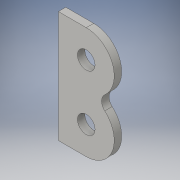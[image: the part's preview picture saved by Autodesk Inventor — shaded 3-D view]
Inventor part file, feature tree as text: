
AUTODESK INVENTOR PART (.ipt)
format: ipt  version: 2016 (Build 200138000, 138)  size: 114,688 bytes
history: native  units: in
note: dims shown in document units (in); Inventor stores cm internally (conversion verified against a paired STEP export)
features: extrude x1, sketch x1
ambient origin geometry x8: Origin, YZ Plane, XZ Plane, XY Plane, X Axis, Y Axis, Z Axis, Center Point
bodies: Solid1 (feature_tree)
feature tree (2):
  extrude  "Extrusion1"  Depth=1.5in
  sketch  "Sketch1"  dims[d2=0.75in d3=1.5in d4=0.375in d5=0.375in d6=0.375in d9=90.0deg d11=0.2362in d12=0.2362in d13=0.375in d14=0.375in d15=0.375in d16=0.375in d17=0.125in d18=0.375in d19=0.1in d20=0.0in]
